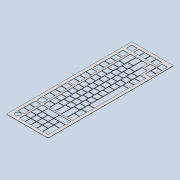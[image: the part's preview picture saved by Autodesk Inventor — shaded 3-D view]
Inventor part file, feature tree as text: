
AUTODESK INVENTOR PART (.ipt)
format: ipt  version: 2021 (Build 250183000, 183)  size: 718,848 bytes
history: native  units: mm
features: extrude x1, sketch x1
ambient origin geometry x8: Origin, YZ Plane, XZ Plane, XY Plane, X Axis, Y Axis, Z Axis, Center Point
bodies: Body1 (feature_tree)
feature tree (2):
  extrude  "Extrusion2"  Depth=19.0mm
  sketch  "Sketch1"  dims[d0=39.05mm d1=19.0mm d2=0.0mm d3=0.0mm d4=19.0mm d5=1.05mm d6=39.05mm d7=19.0mm d8=1.05mm d10=19.0mm d12=19.0mm d13=19.0mm d15=19.0mm d16=19.0mm d17=1.05mm d18=1.05mm d21=19.0mm d25=1.05mm d26=39.05mm d27=19.0mm d33=1.05mm d34=19.0mm d37=24.0125mm d38=5.8125mm d39=24.0125mm d40=24.0125mm d41=1.05mm d42=1.05mm d43=1.05mm d44=1.05mm d45=1.05mm d46=1.05mm d47=19.0mm d48=19.0mm d49=19.0mm d50=118.0mm d51=44.0625mm d52=1.05mm d53=34.0375mm d54=29.025mm d55=19.0mm d56=1.05mm d57=1.05mm d58=1.05mm d59=1.05mm d60=1.05mm d61=1.05mm d62=1.05mm d63=1.05mm d64=1.05mm d66=19.0mm d67=19.0mm d68=19.0mm d69=19.0mm d70=19.0mm d71=19.0mm d72=19.0mm d73=19.0mm d74=19.0mm d75=19.0mm d76=1.05mm d77=1.05mm d78=34.0375mm d79=19.0mm d80=19.0mm d81=1.05mm d82=1.05mm d83=1.05mm d84=1.05mm d85=1.05mm d86=19.0mm d87=19.0mm d88=19.0mm d89=1.05mm d90=1.05mm d91=1.05mm d92=1.05mm d93=1.05mm d94=1.05mm d95=1.05mm d96=19.0mm d97=19.0mm d98=19.0mm d99=19.0mm d100=19.0mm d101=19.0mm d102=44.0625mm d103=1.05mm d104=1.05mm d105=1.05mm d106=1.05mm d107=1.05mm d108=1.05mm d109=1.05mm d110=1.05mm d111=1.05mm d112=1.05mm d116=19.0mm d117=19.0mm d118=19.0mm d119=19.0mm d120=19.0mm d121=19.0mm d122=19.0mm d123=19.0mm d124=19.0mm d125=19.0mm d127=19.0mm d128=19.0mm d129=1.05mm d130=1.05mm d131=29.025mm d132=1.05mm d133=19.0mm d134=19.0mm d135=19.0mm d136=1.05mm d137=1.05mm d138=1.05mm d139=1.05mm d140=1.05mm d141=1.05mm d142=1.05mm d143=1.05mm d144=1.05mm d145=1.05mm d146=1.05mm d147=1.05mm d148=1.05mm d149=39.05mm d150=19.0mm d151=19.0mm d152=19.0mm d153=19.0mm d154=19.0mm d155=19.0mm d156=19.0mm d157=19.0mm d158=19.0mm d159=1.05mm d160=1.05mm d161=1.05mm d162=1.05mm d163=1.05mm d164=1.05mm d165=5.8125mm d166=5.8125mm d168=5.8125mm d169=5.8125mm d170=19.0mm d171=19.0mm d172=19.0mm d173=1.05mm d174=1.05mm d176=1.05mm d178=1.05mm d179=1.05mm d180=1.05mm d181=1.05mm d182=1.05mm d183=19.0mm d184=19.0mm d185=19.0mm d186=19.0mm d187=19.0mm d188=19.0mm d189=19.0mm d191=19.0mm d192=19.0mm d193=19.0mm d194=5.8125mm d195=1.05mm d196=5.8125mm d197=19.0mm d198=19.0mm d199=19.0mm d200=19.0mm d201=19.0mm d202=19.0mm d203=19.0mm d204=1.05mm d205=1.05mm d206=1.05mm d207=19.0mm d208=19.0mm d209=19.0mm d210=19.0mm d211=1.05mm d212=19.0mm d213=19.0mm d214=1.05mm d215=1.05mm d216=19.0mm d218=5.8125mm d219=5.8125mm d220=5.8125mm d221=5.8125mm d223=10.0mm d224=10.0mm d225=10.0mm d226=10.0mm d229=17.05mm d230=10.05mm d231=1.0mm d232=0.0mm]
